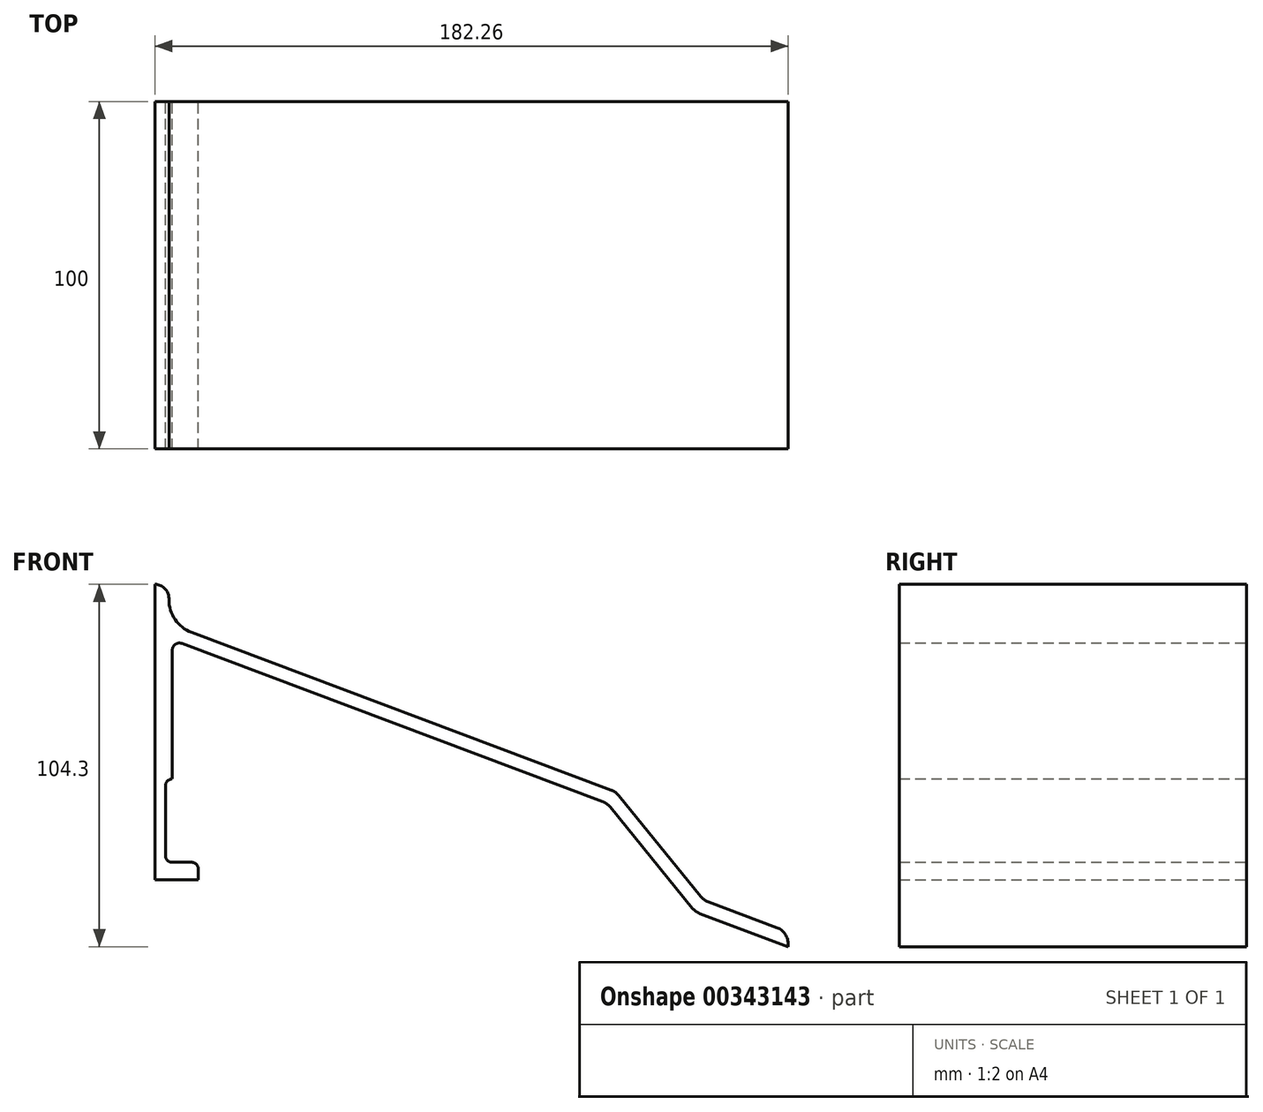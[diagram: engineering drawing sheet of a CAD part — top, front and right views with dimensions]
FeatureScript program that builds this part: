
annotation { "Feature Type Name" : "Feature", "Feature Type Description" : "" }
export const myFeature = defineFeature(function(context is Context, id is Id, definition is map)
    precondition{}
    {
        {
            var Q0;
            Q0=qCreatedBy(makeId("Front.planeOp"),FACE);
            var sketch = newSketch(context, id + "F0", { "sketchPlane" : qUnion([Q0])});
            skLineSegment(sketch, "E0", {"start": v(0, 0) * mm, "end": v(0, 85) * mm});
            skLineSegment(sketch, "E1", {"start": v(0, 0) * mm, "end": v(12.5, 0) * mm});
            skLineSegment(sketch, "E2", {"start": v(12.5, 0) * mm, "end": v(12.5, 3) * mm});
            skLineSegment(sketch, "E3", {"start": v(10.5, 5) * mm, "end": v(5, 5) * mm});
            skLineSegment(sketch, "E4", {"start": v(3, 7) * mm, "end": v(3, 27) * mm});
            skLineSegment(sketch, "E5", {"start": v(5, 29) * mm, "end": v(5, 29) * mm});
            skLineSegment(sketch, "E6", {"start": v(5, 29) * mm, "end": v(5, 66.11) * mm});
            skLineSegment(sketch, "E7", {"start": v(7.7, 67.98) * mm, "end": v(128.94, 22.42) * mm});
            skLineSegment(sketch, "E8", {"start": v(131.06, 20.9) * mm, "end": v(154.74, -8.25) * mm});
            skLineSegment(sketch, "E9.0", {"start": v(10.48, 71.21) * mm, "end": v(131.36, 25.78) * mm});
            skLineSegment(sketch, "E10", {"start": v(0, 85) * mm, "end": v(0, 81) * mm, "construction": true});
            skArc(sketch, "E11", {"start": v(0, 85) * mm, "mid": v(2.83, 83.83) * mm, "end": v(4, 81) * mm});
            skLineSegment(sketch, "E12", {"start": v(4, 81) * mm, "end": v(4, 80.57) * mm});
            skArc(sketch, "E13", {"start": v(4, 80.57) * mm, "mid": v(5.78, 74.88) * mm, "end": v(10.48, 71.21) * mm});
            skLineSegment(sketch, "E14.0", {"start": v(133.48, 24.25) * mm, "end": v(157.16, -4.88) * mm});
            skLineSegment(sketch, "E15", {"start": v(159.28, -6.41) * mm, "end": v(179.02, -13.83) * mm});
            skLineSegment(sketch, "E16.0", {"start": v(156.86, -9.77) * mm, "end": v(182.2, -19.3) * mm});
            skArc(sketch, "E17", {"start": v(179.02, -13.83) * mm, "mid": v(181.59, -16) * mm, "end": v(182.2, -19.3) * mm});
            skPoint(sketch, "E18.visualSharp", {"position": v(158.01, -5.94) * mm});
            skArc(sketch, "E18.filletArc", {"start": v(157.16, -4.88) * mm, "mid": v(158.12, -5.79) * mm, "end": v(159.28, -6.41) * mm});
            skPoint(sketch, "E19.visualSharp", {"position": v(155.6, -9.3) * mm});
            skArc(sketch, "E19.filletArc", {"start": v(154.74, -8.25) * mm, "mid": v(155.7, -9.15) * mm, "end": v(156.86, -9.77) * mm});
            skPoint(sketch, "E20.visualSharp", {"position": v(132.63, 25.3) * mm});
            skArc(sketch, "E20.filletArc", {"start": v(133.48, 24.25) * mm, "mid": v(132.52, 25.16) * mm, "end": v(131.36, 25.78) * mm});
            skPoint(sketch, "E21.visualSharp", {"position": v(130.2, 21.94) * mm});
            skArc(sketch, "E21.filletArc", {"start": v(131.06, 20.9) * mm, "mid": v(130.1, 21.8) * mm, "end": v(128.94, 22.42) * mm});
            skPoint(sketch, "E22.visualSharp", {"position": v(5, 69) * mm});
            skArc(sketch, "E22.filletArc", {"start": v(7.7, 67.98) * mm, "mid": v(5.86, 67.76) * mm, "end": v(5, 66.11) * mm});
            skPoint(sketch, "E23.visualSharp", {"position": v(3, 29) * mm});
            skArc(sketch, "E23.filletArc", {"start": v(5, 29) * mm, "mid": v(3.59, 28.41) * mm, "end": v(3, 27) * mm});
            skPoint(sketch, "E24.visualSharp", {"position": v(3, 5) * mm});
            skArc(sketch, "E24.filletArc", {"start": v(3, 7) * mm, "mid": v(3.59, 5.59) * mm, "end": v(5, 5) * mm});
            skPoint(sketch, "E25.visualSharp", {"position": v(12.5, 5) * mm});
            skArc(sketch, "E25.filletArc", {"start": v(12.5, 3) * mm, "mid": v(11.91, 4.41) * mm, "end": v(10.5, 5) * mm});
            skSolve(sketch);
        }
        {
            var Q0;
            Q0=makeQuery(id+"F0.imprint","IMPRINT",FACE,{"disambiguationData":[TD([[makeQuery(id+"F0.imprint","IMPRINT",EDGE,{"derivedFrom":sQuery(id+"F0.wireOp",EDGE,"E0")}),-1.0]])]});
            extrude(context, id + "F1", {"entities" : qUnion([Q0]), "depth" : 100 * mm});
        }
    });
